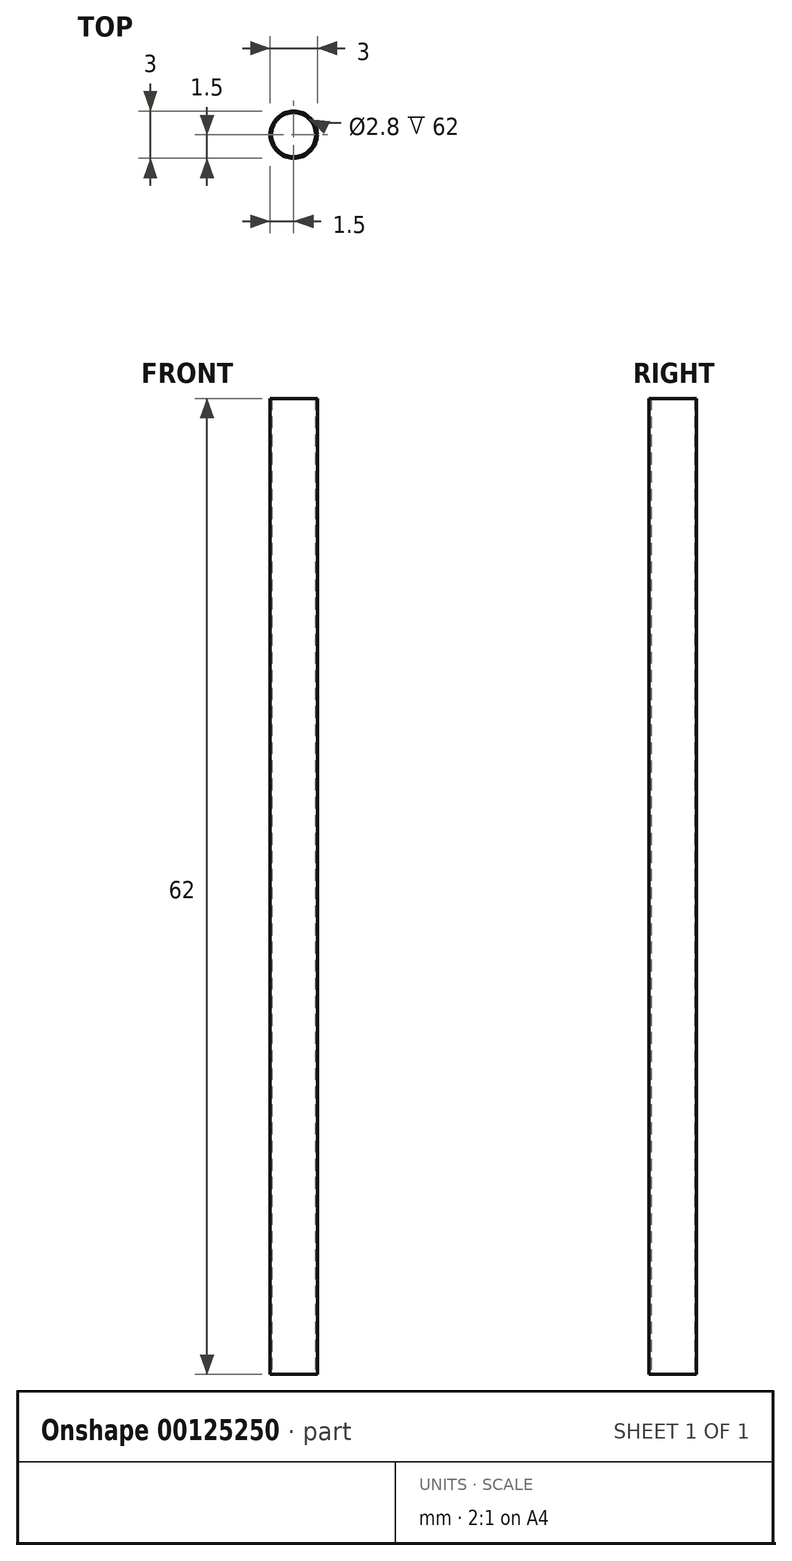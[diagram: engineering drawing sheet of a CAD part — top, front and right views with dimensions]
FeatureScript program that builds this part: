
annotation { "Feature Type Name" : "Feature", "Feature Type Description" : "" }
export const myFeature = defineFeature(function(context is Context, id is Id, definition is map)
    precondition{}
    {
        {
            var Q0;
            Q0=qCreatedBy(makeId("Top.planeOp"),FACE);
            var sketch = newSketch(context, id + "F0", { "sketchPlane" : qUnion([Q0])});
            skCircle(sketch, "E0", {"center": v(0, 0) * mm, "radius": 1.5 * mm});
            skCircle(sketch, "E1", {"center": v(0, 0) * mm, "radius": 1.4 * mm});
            skSolve(sketch);
        }
        {
            var Q0;
            Q0=makeQuery(id+"F0.imprint","IMPRINT",FACE,{"disambiguationData":[TD([[makeQuery(id+"F0.imprint","IMPRINT",EDGE,{"derivedFrom":sQuery(id+"F0.wireOp",EDGE,"E0")}),1.0]])]});
            extrude(context, id + "F1", {"entities" : qUnion([Q0]), "depth" : 62 * mm});
        }
    });
